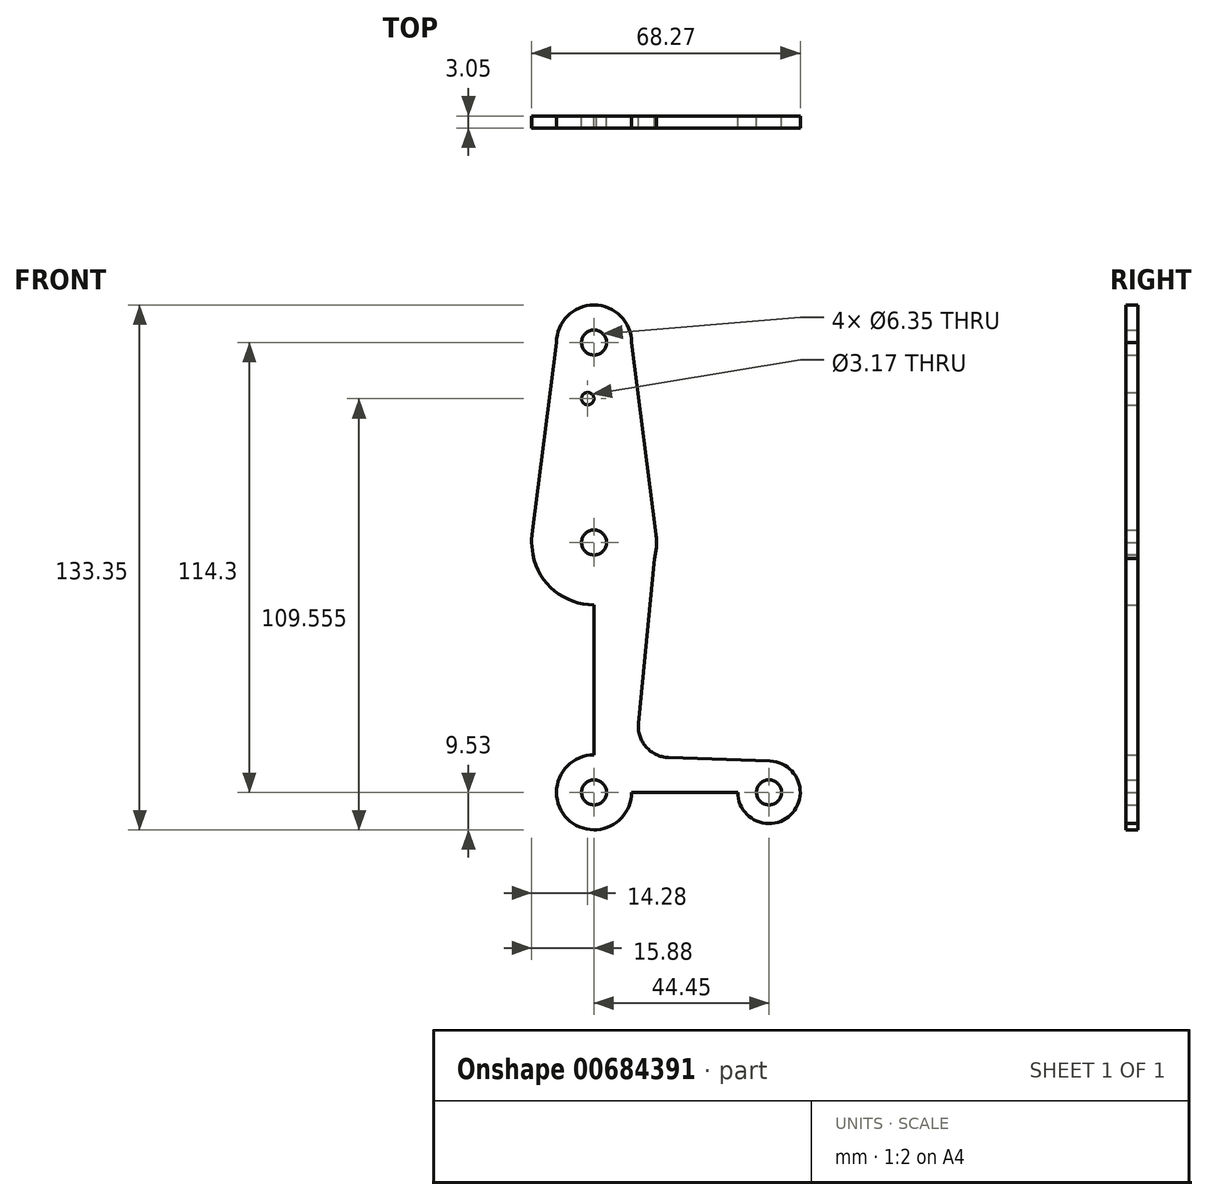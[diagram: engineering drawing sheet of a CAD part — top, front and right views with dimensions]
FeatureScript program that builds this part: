
annotation { "Feature Type Name" : "Feature", "Feature Type Description" : "" }
export const myFeature = defineFeature(function(context is Context, id is Id, definition is map)
    precondition{}
    {
        {
            var Q0;
            Q0=qCreatedBy(makeId("Front.planeOp"),FACE);
            var sketch = newSketch(context, id + "F0", { "sketchPlane" : qUnion([Q0])});
            skCircle(sketch, "E0", {"center": v(0, 0) * mm, "radius": 15.88 * mm});
            skCircle(sketch, "E1", {"center": v(0, 50.8) * mm, "radius": 9.53 * mm});
            skCircle(sketch, "E2", {"center": v(0, -63.5) * mm, "radius": 9.53 * mm});
            skCircle(sketch, "E3", {"center": v(44.45, -63.5) * mm, "radius": 7.94 * mm});
            skLineSegment(sketch, "E4", {"start": v(0, 50.8) * mm, "end": v(0, -63.5) * mm});
            skLineSegment(sketch, "E5", {"start": v(0, -63.5) * mm, "end": v(44.45, -63.5) * mm});
            skLineSegment(sketch, "E6", {"start": v(-9.52, 50.8) * mm, "end": v(-15.75, 2) * mm});
            skLineSegment(sketch, "E7", {"start": v(9.53, 50.8) * mm, "end": v(15.75, 2) * mm});
            skLineSegment(sketch, "E8", {"start": v(-15.88, 0) * mm, "end": v(-9.48, -64.44) * mm});
            skLineSegment(sketch, "E9", {"start": v(15.75, 0) * mm, "end": v(11.28, -45.93) * mm});
            skLineSegment(sketch, "E10", {"start": v(18.9, -54.65) * mm, "end": v(44.73, -55.57) * mm});
            skLineSegment(sketch, "E11", {"start": v(0, -73.03) * mm, "end": v(44.73, -71.43) * mm});
            skPoint(sketch, "E12.newPointA", {"position": v(9.48, -64.44) * mm});
            skArc(sketch, "E12.filletArc", {"start": v(11.28, -45.93) * mm, "mid": v(13.21, -51.94) * mm, "end": v(18.9, -54.65) * mm});
            skCircle(sketch, "E13", {"center": v(0, 50.8) * mm, "radius": 3.18 * mm});
            skCircle(sketch, "E14", {"center": v(0, 0) * mm, "radius": 3.18 * mm});
            skCircle(sketch, "E15", {"center": v(0, -63.5) * mm, "radius": 3.18 * mm});
            skCircle(sketch, "E16", {"center": v(44.45, -63.5) * mm, "radius": 3.18 * mm});
            skLineSegment(sketch, "E17", {"start": v(0, 0) * mm, "end": v(0, 36.53) * mm});
            skCircle(sketch, "E18", {"center": v(-1.6, 36.53) * mm, "radius": 1.59 * mm});
            skSolve(sketch);
        }
        {
            var Q0;
            Q0=makeQuery(id+"F0.imprint","IMPRINT",FACE,{"disambiguationData":[TD([[makeQuery(id+"F0.imprint","IMPRINT",EDGE,{"derivedFrom":sQuery(id+"F0.wireOp",EDGE,"E13")}),-1.0]])]});
            var Q1;
            {var subQ0=sQuery(id+"F0.wireOp",EDGE,"E7");Q1=makeQuery(id+"F0.imprint","IMPRINT",FACE,{"disambiguationData":[TD([[makeQuery(id+"F0.imprint","IMPRINT",EDGE,{"derivedFrom":subQ0}),-1.0]])]});}
            var Q2;
            {var subQ0=sQuery(id+"F0.wireOp",EDGE,"E6");Q2=makeQuery(id+"F0.imprint","IMPRINT",FACE,{"disambiguationData":[TD([[makeQuery(id+"F0.imprint","IMPRINT",EDGE,{"derivedFrom":subQ0}),1.0]])]});}
            var Q3;
            {var subQ1=sQuery(id+"F0.wireOp",EDGE,"E0");var subQ9=makeQuery(id+"F0.imprint","INTERSECT",VERTEX,{"derivedFrom":[subQ1,sQuery(id+"F0.wireOp",EDGE,"E6")]});Q3=makeQuery(id+"F0.imprint","IMPRINT",FACE,{"disambiguationData":[TD([[makeQuery(id+"F0.imprint","IMPRINT",EDGE,{"disambiguationData":[TD([[subQ9,1.0]])],"derivedFrom":subQ1}),1.0]])]});}
            var Q4;
            {var subQ1=sQuery(id+"F0.wireOp",EDGE,"E0");var subQ5=makeQuery(id+"F0.imprint","INTERSECT",VERTEX,{"derivedFrom":[subQ1,sQuery(id+"F0.wireOp",EDGE,"E7")]});Q4=makeQuery(id+"F0.imprint","IMPRINT",FACE,{"disambiguationData":[TD([[makeQuery(id+"F0.imprint","IMPRINT",EDGE,{"disambiguationData":[TD([[subQ5,-1.0]])],"derivedFrom":subQ1}),1.0]])]});}
            var Q5;
            {var subQ5=sQuery(id+"F0.wireOp",EDGE,"E10");Q5=makeQuery(id+"F0.imprint","IMPRINT",FACE,{"disambiguationData":[TD([[makeQuery(id+"F0.imprint","IMPRINT",EDGE,{"derivedFrom":subQ5}),-1.0]])]});}
            var Q6;
            {var subQ0=sQuery(id+"F0.wireOp",EDGE,"E8");var subQ1=sQuery(id+"F0.wireOp",EDGE,"E0");var subQ2=makeQuery(id+"F0.imprint","INTERSECT",VERTEX,{"disambiguationData":[OD(1.0)],"derivedFrom":[subQ1,subQ0]});Q6=makeQuery(id+"F0.imprint","IMPRINT",FACE,{"disambiguationData":[TD([[makeQuery(id+"F0.imprint","IMPRINT",EDGE,{"disambiguationData":[TD([[subQ2,-1.0]])],"derivedFrom":subQ1}),-1.0]])]});}
            var Q7;
            {var subQ1=sQuery(id+"F0.wireOp",EDGE,"E2");var subQ5=makeQuery(id+"F0.imprint","INTERSECT",VERTEX,{"derivedFrom":[subQ1,sQuery(id+"F0.wireOp",EDGE,"E8")]});Q7=makeQuery(id+"F0.imprint","IMPRINT",FACE,{"disambiguationData":[TD([[makeQuery(id+"F0.imprint","IMPRINT",EDGE,{"disambiguationData":[TD([[subQ5,1.0]])],"derivedFrom":subQ1}),1.0]])]});}
            var Q8;
            {var subQ0=sQuery(id+"F0.wireOp",EDGE,"E4");var subQ1=sQuery(id+"F0.wireOp",EDGE,"E2");var subQ2=makeQuery(id+"F0.imprint","INTERSECT",VERTEX,{"derivedFrom":[subQ1,subQ0]});Q8=makeQuery(id+"F0.imprint","IMPRINT",FACE,{"disambiguationData":[TD([[makeQuery(id+"F0.imprint","IMPRINT",EDGE,{"disambiguationData":[TD([[subQ2,1.0]])],"derivedFrom":subQ1}),1.0]])]});}
            var Q9;
            {var subQ0=sQuery(id+"F0.wireOp",EDGE,"E11");var subQ1=sQuery(id+"F0.wireOp",EDGE,"E2");var subQ2=makeQuery(id+"F0.imprint","INTERSECT",VERTEX,{"disambiguationData":[OD(1.0)],"derivedFrom":[subQ1,subQ0]});Q9=makeQuery(id+"F0.imprint","IMPRINT",FACE,{"disambiguationData":[TD([[makeQuery(id+"F0.imprint","IMPRINT",EDGE,{"disambiguationData":[TD([[subQ2,-1.0]])],"derivedFrom":subQ1}),-1.0]])]});}
            var Q10;
            Q10=makeQuery(id+"F0.imprint","IMPRINT",FACE,{"disambiguationData":[TD([[makeQuery(id+"F0.imprint","IMPRINT",EDGE,{"derivedFrom":sQuery(id+"F0.wireOp",EDGE,"E16")}),-1.0]])]});
            extrude(context, id + "F1", {"entities" : qUnion([Q0, Q1, Q2, Q3, Q4, Q5, Q6, Q7, Q8, Q9, Q10]), "depth" : 3.05 * mm, "offsetDistance" : 25.4 * mm});
        }
    });
